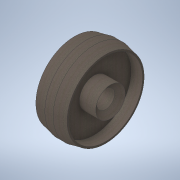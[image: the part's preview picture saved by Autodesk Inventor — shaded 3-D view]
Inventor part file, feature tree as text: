
AUTODESK INVENTOR PART (.ipt)
format: ipt  version: 2020 (Build 240168000, 168)  size: 154,112 bytes
history: native  units: mm
features: revolve x1, sketch x1
ambient origin geometry x8: Origin, YZ Plane, XZ Plane, XY Plane, X Axis, Y Axis, Z Axis, Center Point
bodies: Solid1 (feature_tree)
feature tree (2):
  revolve  "Revolution1"  [1 undecoded]
  sketch  "Sketch1"  dims[d0=50.0mm d1=18.0mm d2=38.0mm d3=11.0mm d4=39.0mm d5=27.0mm d8=10.0mm d9=20.0mm d10=90.0deg d11=34.0mm d12=2.0mm d13=2.0mm d14=18.0mm d15=26.248585mm d16=11.714245mm d17=18.0mm d18=45.0mm]
note: 1 required parameter value undecoded (feature->parameter linkage not recoverable at this tier; creation-order binding heuristic only, values carry confidence <= 0.55)
